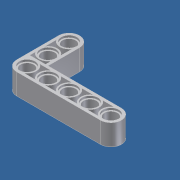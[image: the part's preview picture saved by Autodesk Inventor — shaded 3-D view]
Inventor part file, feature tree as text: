
AUTODESK INVENTOR PART (.ipt)
format: ipt  version: unknown  size: 346,112 bytes
history: native  units: mm
features: extrude x7, sketch x7
ambient origin geometry x8: Origin, YZ Plane, XZ Plane, XY Plane, X Axis, Y Axis, Z Axis, Center Point
bodies: Solid1 (feature_tree)
feature tree (14):
  extrude  "Extrusion1"  Depth=4.0mm
  extrude  "Extrusion2"  Depth=32.0mm
  extrude  "Extrusion3"  TaperAngle=0.0deg  [1 undecoded]
  extrude  "Extrusion4"  Depth=16.0mm
  extrude  "Extrusion5"  Depth=4.0mm
  extrude  "Extrusion6"  Depth=8.0mm TaperAngle=0.0deg
  extrude  "Extrusion7"  Depth=10.0mm
  sketch  "Sketch1"  dims[d3=4.0mm d4=4.0mm]
  sketch  "Sketch2"  dims[d5=4.0mm d6=32.0mm]
  sketch  "Sketch3"  dims[d7=16.0mm d10=0.0mm]
  sketch  "Sketch4"  dims[d12=90.0deg d13=16.0mm]
  sketch  "Sketch5"  dims[d14=4.0mm d15=4.0mm]
  sketch  "Sketch6"  dims[d16=16.0mm d17=8.0mm d18=0.0mm]
  sketch  "Sketch7"  dims[d19=5.0mm d20=10.0mm d22=10.0mm d23=50.0mm d25=8.0mm d27=8.0mm d28=0.0mm d29=5.0mm d30=10.0mm d32=10.0mm d33=20.0mm d35=8.0mm d37=8.0mm d38=0.0mm d39=6.0mm d40=6.0mm d41=6.0mm d42=6.0mm d43=6.0mm d44=6.0mm d45=6.0mm d46=0.8mm d47=0.0mm d48=6.0mm d49=6.0mm d50=6.0mm d51=6.0mm d52=6.0mm d53=6.0mm d54=6.0mm d55=0.8mm d56=0.0mm d57=7.0mm d58=7.0mm d59=10.0mm d61=10.0mm d62=40.0mm d64=8.0mm d66=10.0mm d67=0.0mm d68=7.0mm d69=7.0mm d70=3.5mm d71=3.5mm d72=2.197224mm d73=6.0mm d74=10.0mm d75=0.0mm]
note: 1 required parameter value undecoded (feature->parameter linkage not recoverable at this tier; creation-order binding heuristic only, values carry confidence <= 0.55)
